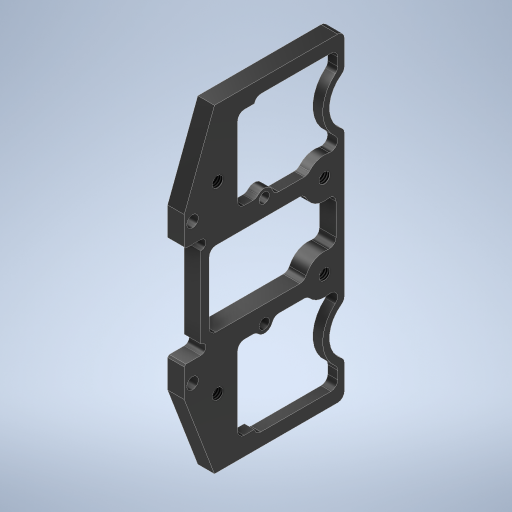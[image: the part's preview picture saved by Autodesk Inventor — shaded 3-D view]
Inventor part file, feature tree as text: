
AUTODESK INVENTOR PART (.ipt)
format: ipt  version: 2024.2 (Build 282272000, 272)  size: 501,760 bytes
history: native  units: mm
features: extrude x2, hole x2, other x1, mirror x1, chamfer x1, sketch x1
ambient origin geometry x8: Origin, YZ Plane, XZ Plane, XY Plane, X Axis, Y Axis, Z Axis, Center Point
bodies: Solid1 (feature_tree)
feature tree (8):
  other  "KneeFrameBasis.ipt"
  extrude  "Extrusion1"  Depth=5.0mm TaperAngle=0.0deg
  extrude  "Extrusion2"  Depth=2.0mm TaperAngle=0.0deg
  hole  "Phi3.1"  [1 undecoded]
  hole  "Phi3.5"  [1 undecoded]
  mirror  "Mirror1"
  chamfer  "C0.5"  Distance=0.5mm Angle=45.0deg
  sketch  "Sketch1"  dims[d0=10.0mm d1=5.0mm d2=0.0mm d3=2.0mm d4=0.0mm d7=3.242mm d8=8.0mm d9=4.0mm d10=2.0mm d11=90.0deg d12=11.8mm d13=0.0mm d14=3.1mm d15=8.0mm d16=4.0mm d17=2.0mm d18=90.0deg d19=8.0mm d20=20.594885mm d21=3.5mm d22=6.0mm d23=4.0mm d24=2.0mm d25=90.0deg d26=8.0mm d27=20.594885mm d28=2.0mm d29=0.0mm d30=0.0mm d31=0.5mm d32=2.0mm d33=45.0deg]
note: 2 required parameter values undecoded (feature->parameter linkage not recoverable at this tier; creation-order binding heuristic only, values carry confidence <= 0.55)
